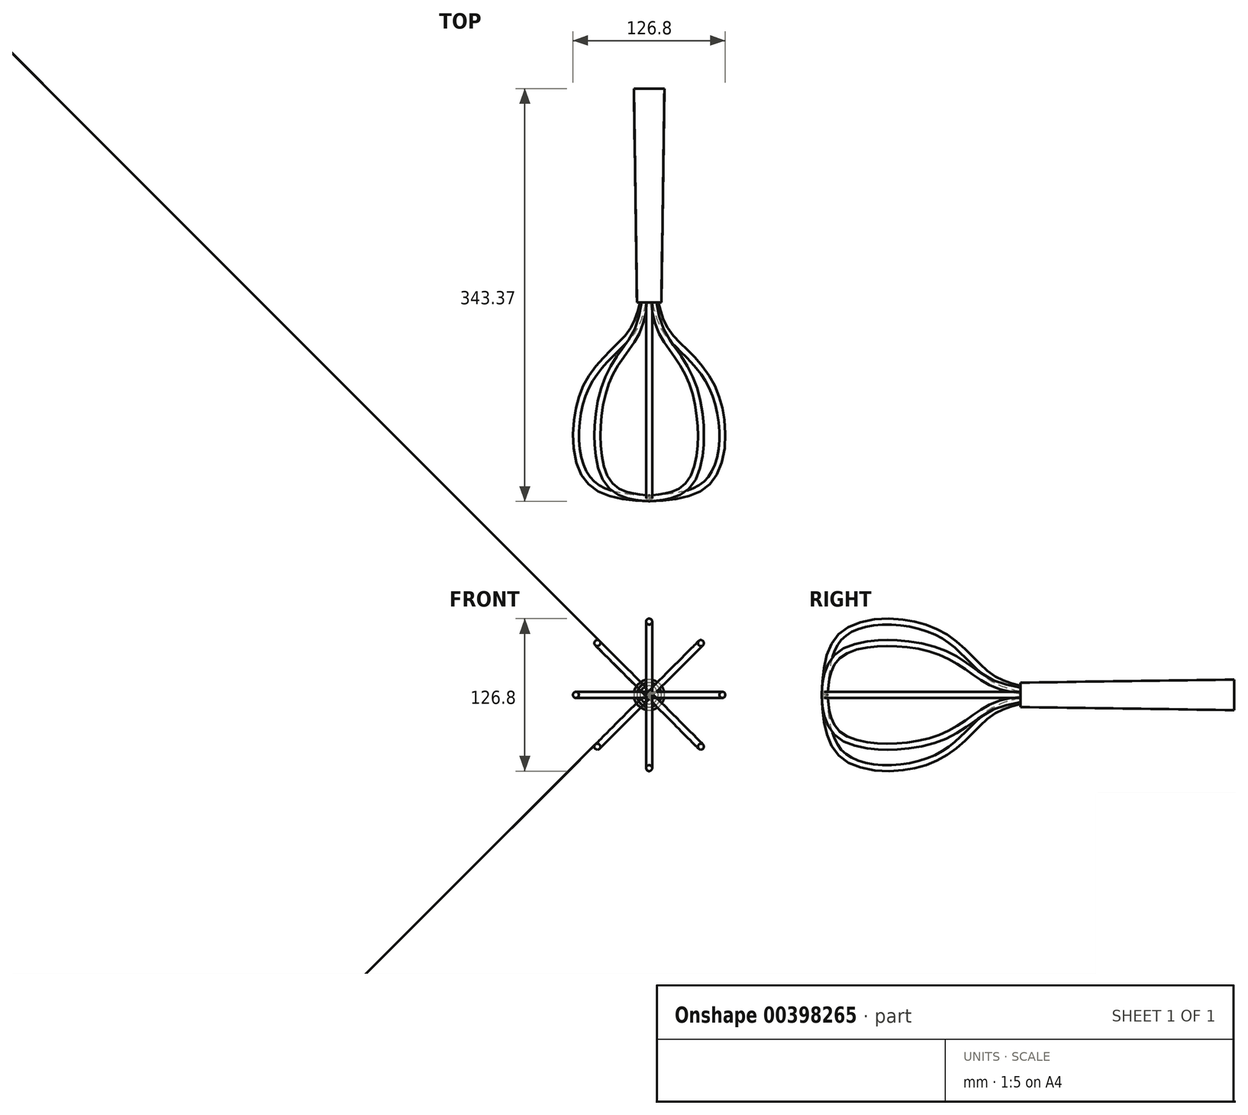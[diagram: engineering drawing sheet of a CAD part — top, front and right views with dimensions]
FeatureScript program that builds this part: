
annotation { "Feature Type Name" : "Feature", "Feature Type Description" : "" }
export const myFeature = defineFeature(function(context is Context, id is Id, definition is map)
    precondition{}
    {
        {
            var Q0;
            Q0=qCreatedBy(makeId("Front.planeOp"),FACE);
            var sketch = newSketch(context, id + "F0", { "sketchPlane" : qUnion([Q0])});
            skCircle(sketch, "E0", {"center": v(0, 0) * mm, "radius": 12.7 * mm});
            skSolve(sketch);
        }
        {
            var Q0;
            Q0=qCreatedBy(makeId("Front.planeOp"),FACE);
            cPlane(context, id + "F1", {"entities" : qUnion([Q0]), "cplaneType" : CPlaneType.OFFSET, "offset" : 177.8 * mm, "width" : 152.4 * mm, "height" : 152.4 * mm});
        }
        {
            var Q0;
            Q0=qCreatedBy(id+"F1.planeOp",FACE);
            var sketch = newSketch(context, id + "F2", { "sketchPlane" : qUnion([Q0])});
            skCircle(sketch, "E1", {"center": v(0, 0) * mm, "radius": 10.16 * mm});
            skSolve(sketch);
        }
        {
            var Q0;
            Q0=makeQuery(id+"F0.imprint","IMPRINT",FACE,{"disambiguationData":[TD([[makeQuery(id+"F0.imprint","IMPRINT",EDGE,{"derivedFrom":sQuery(id+"F0.wireOp",EDGE,"E0")}),1.0]])]});
            var Q1;
            Q1=makeQuery(id+"F2.imprint","IMPRINT",FACE,{"disambiguationData":[TD([[makeQuery(id+"F2.imprint","IMPRINT",EDGE,{"derivedFrom":sQuery(id+"F2.wireOp",EDGE,"E1")}),1.0]])]});
            loft(context, id + "F3", {"sheetProfilesArray" : [{ "sheetProfileEntities" : qUnion([Q0]) }, { "sheetProfileEntities" : qUnion([Q1]) }]});
        }
        {
            var Q0;
            Q0=makeQuery(id+"F3.opLoft","CAP_FACE",FACE,{"disambiguationData":[OSD([makeQuery(id+"F2.imprint","IMPRINT",FACE,{"disambiguationData":[TD([[makeQuery(id+"F2.imprint","IMPRINT",EDGE,{"derivedFrom":sQuery(id+"F2.wireOp",EDGE,"E1")}),1.0]])]})])],"isStart":true});
            var sketch = newSketch(context, id + "F4", { "sketchPlane" : qUnion([Q0])});
            skCircle(sketch, "E2", {"center": v(0, 5.08) * mm, "radius": 2.54 * mm});
            skSolve(sketch);
        }
        {
            var Q0;
            Q0=qCreatedBy(makeId("Right.planeOp"),FACE);
            var sketch = newSketch(context, id + "F5", { "sketchPlane" : qUnion([Q0])});
            skPoint(sketch, "E3.0", {"position": v(-177.8, 5.08) * mm});
            skFitSpline(sketch, "E4", {"points": [v(-177.8, 5.08) * mm, v(-204.3, 15.98) * mm, v(-247.81, 52.23) * mm, v(-323.95, 51.63) * mm, v(-340.87, 0) * mm], "startDerivative": vector(-145.68, 36.02) * mm, "endDerivative": vector(-14.64, -241.05) * mm});
            skSolve(sketch);
        }
        {
            var Q0;
            Q0=makeQuery(id+"F4.imprint","IMPRINT",FACE,{"disambiguationData":[TD([[makeQuery(id+"F4.imprint","IMPRINT",EDGE,{"derivedFrom":sQuery(id+"F4.wireOp",EDGE,"E2")}),1.0]])]});
            var Q1;
            Q1=sQuery(id+"F5.wireOp",EDGE,"E4");
            sweep(context, id + "F6", {"operationType" : NewBodyOperationType.ADD, "profiles" : qUnion([Q0]), "path" : qUnion([Q1])});
        }
        {
            var Q0;
            Q0=qCreatedBy(makeId("Top.planeOp"),FACE);
            var sketch = newSketch(context, id + "F7", { "sketchPlane" : qUnion([Q0])});
            skLineSegment(sketch, "E5", {"start": v(0, -71) * mm, "end": v(0, -189.4) * mm, "construction": true});
            skSolve(sketch);
        }
        {
            var Q0;
            Q0=makeQuery(id+"F3.opLoft","SWEPT_BODY",BODY,{"disambiguationData":[OSD([makeQuery(id+"F0.imprint","IMPRINT",FACE,{"disambiguationData":[TD([[makeQuery(id+"F0.imprint","IMPRINT",EDGE,{"derivedFrom":sQuery(id+"F0.wireOp",EDGE,"E0")}),1.0]])]}),makeQuery(id+"F2.imprint","IMPRINT",FACE,{"disambiguationData":[TD([[makeQuery(id+"F2.imprint","IMPRINT",EDGE,{"derivedFrom":sQuery(id+"F2.wireOp",EDGE,"E1")}),1.0]])]})])]});
            var Q1;
            Q1=sQuery(id+"F7.wireOp",EDGE,"E5");
            circularPattern(context, id + "F8", {"entities" : qUnion([Q0]), "axis" : qUnion([Q1]), "angle" : 360 * degree, "instanceCount" : 8, "equalSpace" : true});
        }
    });
